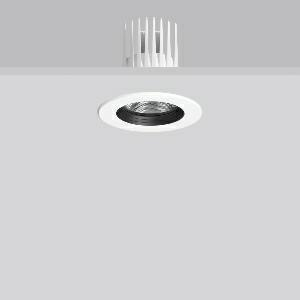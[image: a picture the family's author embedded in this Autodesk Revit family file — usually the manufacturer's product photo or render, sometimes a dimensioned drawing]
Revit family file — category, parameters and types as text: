
# Revit family: heledon_mini_e_901742_002_3_b000
name_source: partatom
category: Lighting Fixtures
units: mm (PartAtom-declared; Revit-internal decimal feet)

## family parameters
Cut with Voids When Loaded = No
Host = Face
Light Source = No
Part Type = Normal
Room Calculation Point = No
Round Connector Dimension = Use Diameter
Shared = No

## types (1)
- HELEDON mini E (1 x LED Modul 935, 2650 lm, 3500)
    Apparent Load = 20 VA
    Approval mark = CE
    CIE Flux Codes = 95 99 100 100 100
    Color Rendering = 92
    Color Temperature = 3500
    Default Elevation = 1800 mm
    Description = Series: HELEDON mini
Round recessed downlight. Housing: die-cast aluminium, powder-coated. Black plastic ring and recessed LED to prevent glare from the side. Optical assembly with reflector made of MIRO-Silver with 98% total light reflection for outstanding efficiency - can be changed without tools. Best colour rendering index Ra>90. Suitable for Recessed ceiling mounting. Installation without tools thanks to spring fastening system. Including separate LED converter with connecting cable 600 mm.High quality converter without flickering and stroboscopic effect. Through-wiring box (5 pole) available as accessory. The following accessories can be mounted without use of tools: interchangeable lenses, decorative glasses, honeycomb louvre, clear and frosted diffusers, white interchangeable plastic ring. 
Colour: traffic white, matt (RAL 9016)
Diameter: 124 mm
Height: 3 mm
Cut-out diameter: 114 mm
Recess height: 170 mm
Luminaire: recess height: 120 mm
Lamp: LED
Socket: without socket
Colour temperature: 3500K
Colour rendering index (CRI): 92
System power: 20 W
Rated luminous flux: 2650 lm
Luminous efficiency: 133 lm/W
Control gear: Regulated power supply
Protection class: II
Type of protection: IP 20
    Height = 0 mm  [stored 0 ft]
    Lamp = 1 x LED Modul 935
    Lamp Light Flux = 2650 lm
    Lamp count = 1
    Length = 124 mm  [stored 0.406824 ft]
    Lifetime = 50000 h
    Luminous efficacy = 133 lm/W
    Manufacturer = RZB
    ModVariant = No
    Model = 901742.002.3
    Mounting Place = Ceiling
    Mounting Type = Recessed
    Number of Poles = 1
    OnlyDefault = Yes
    Power Factor = 1
    Product Name = HELEDON mini E
    Product group = Recessed downlights
    ProductGroupID = 402
    Protection Class = Protection class II
    Protection Degree = IP 20
    RLX_Detail_Level = 1
    RLX_Emergency_Light_Flux = 0 lm
    RLX_Emergency_Type = 0
    RLX_Emergency_Type_DB = No
    RlxData = <blob elided: 123321 chars, md5=fe10db97>
    Socket = socket
    Standby Power = 0 W
    System Light Flux = 2650 lm
    System Power = 20 W
    Type Comments = Product without accessories
    Type Image = 901657.002.jpg
    URL = http://relux.com
    VarID = ---
    Voltage = 230 V
    Voltage Range = 220-240 V
    Weight = 0.00 kg
    Width = 0 mm  [stored 0 ft]

note: [stored X ft] marks values corroborated as IEEE doubles in the binary element streams (Revit-internal decimal feet)

## geometry (parser evidence)
native form markers: Blend x4, Sweep x12
no freeform markers — native parametric forms only
